# Revit family: Bath_Single-Lever-GROHE-Defined-29302_Series
name_source: partatom
category: Plumbing Fixtures
units: mm (PartAtom-declared; Revit-internal decimal feet)

## family parameters
Always vertical = No
Cut with Voids When Loaded = No
OmniClass Number = 23.45.55.14
OmniClass Title = Single Faucets
Part Type = Normal
Room Calculation Point = No
Round Connector Dimension = Use Diameter
Shared = Yes
Work Plane-Based = Yes

## types (2) — shared parameters
Assembly Code = D2020300
CEC Compliant = Yes
CW Connection = No
CWFU = 3
CalGreen Compliant = Yes
Compliance Certifications = • CEC Certified • CALGreen Compliant • Massachusetts Plumbing Board Approved • Energy Policy Act of 1992• CSA B125.1• ASME A112.18.1
Default Elevation = 0"
Description = Single-Handle Freestanding Tub Faucet with 1.75 GPM Hand Shower
Flow Rate = 1.75 gal (US)/min
HW Connection = No
HWFU = 3
Height = 33 9/16"
Height Constatraint = 33 9/16"
Installation Type = Floor Mounted
Length = 11 9/16"
Manufacturer = GROHE
Product Documentation Link = https://americanstandard.box.com
Product Page URL = https://www.grohe.us
Revised Date = 06/06/2023
Tempered Water Connection = Yes
Tempered Water Connection Diameter = 1/2"
URL = https://www.grohe.us
Vent Connection = No
Warranty Information = Limited lifetime warranty
Waste Connection = No
Width = 4 3/4"
zero-valued in all types: WFU

## per-type parameters (varying)
| type | Finish | Material |
| 29302000 | Metal-Grohe-000-Starlight Chrome | Metal-Grohe-000-Starlight Chrome |
| 29302EN0 | Metal-Grohe-EN0-Brushed Nickel | Metal-Grohe-EN0-Brushed Nickel |

note: column(s) folded — value = type name in every type: Model

## geometry (parser evidence)
native form markers: Sweep x2
no freeform markers — native parametric forms only
